SOLIDWORKS PART (.sldprt)
format: sldprt  version: not decoded by parser v0  size: 133,632 bytes
history: native  units: mm
features: plane x3, sketch x3, extrude x2, material x1, revolve x1, fillet x1 (+10 scaffold rows collapsed)
feature tree (21):
  scaffold x10  (default folders/planes/origin — collapsed)
  material  "Material <not specified>"
  plane  "Piano frontale"
  plane  "Piano superiore"
  plane  "Piano destro"
  sketch  "Sketch2"
  revolve  "Revolve1"  Angle=360deg
  sketch  "Sketch3"  dims[D1=320.0mm D2=320.0mm D3=320.0mm D4=320.0mm]
  extrude  "Boss-Extrude1"  Depth=20mm
  fillet  "Fillet1"  Radius=60mm
  sketch  "Sketch4"
  extrude  "Boss-Extrude2"  Depth=20mm
decode coverage: 5 of 7 modeling features carry decoded parameters
note: suppression state not decoded; provenance and decode notes live in map.json
